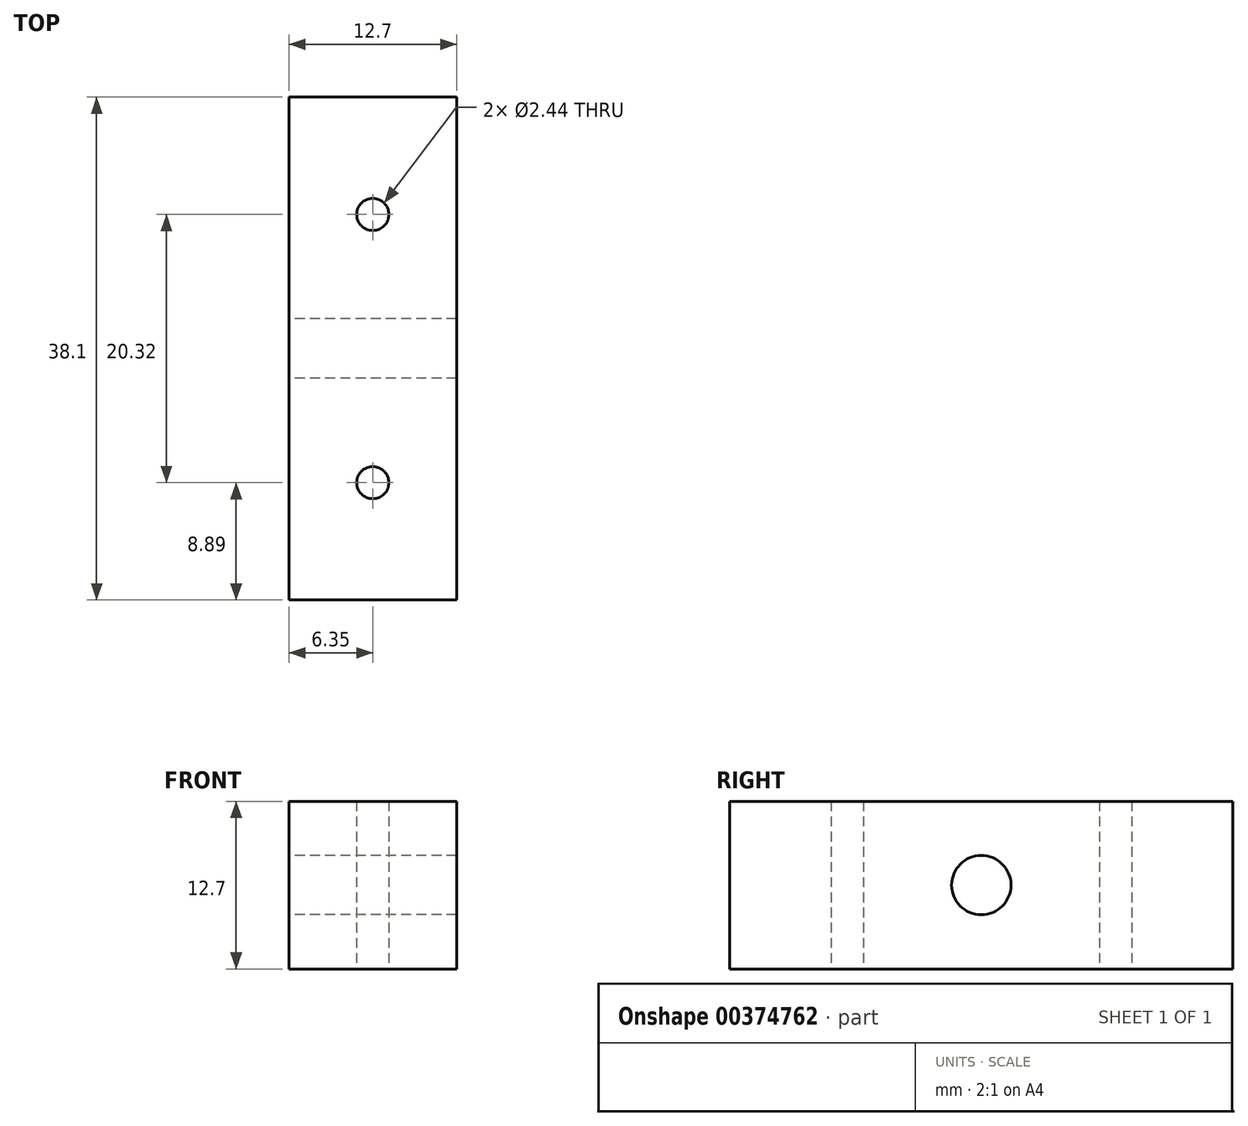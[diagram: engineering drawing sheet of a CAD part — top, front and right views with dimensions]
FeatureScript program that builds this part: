
annotation { "Feature Type Name" : "Feature", "Feature Type Description" : "" }
export const myFeature = defineFeature(function(context is Context, id is Id, definition is map)
    precondition{}
    {
        {
            var Q0;
            Q0=qCreatedBy(makeId("Top.planeOp"),FACE);
            var sketch = newSketch(context, id + "F0", { "sketchPlane" : qUnion([Q0])});
            skLineSegment(sketch, "E0.bottom", {"start": v(12.7, -19.05) * mm, "end": v(0, -19.05) * mm});
            skLineSegment(sketch, "E0.top", {"start": v(12.7, 19.05) * mm, "end": v(0, 19.05) * mm});
            skLineSegment(sketch, "E0.left", {"start": v(12.7, -19.05) * mm, "end": v(12.7, 19.05) * mm});
            skLineSegment(sketch, "E0.right", {"start": v(0, -19.05) * mm, "end": v(0, 19.05) * mm});
            skSolve(sketch);
        }
        {
            var Q0;
            Q0 = qSketchRegion(id + "F0", true);
            extrude(context, id + "F1", {"entities" : qUnion([Q0]), "depth" : 12.7 * mm});
        }
        {
            var Q0;
            Q0=qCreatedBy(makeId("Right.planeOp"),FACE);
            var sketch = newSketch(context, id + "F2", { "sketchPlane" : qUnion([Q0])});
            skPoint(sketch, "E1", {"position": v(0, 6.35) * mm});
            skSolve(sketch);
        }
        {
            var Q0;
            Q0=sQuery(id+"F2.wireOp",VERTEX,"E1");
            var Q1;
            Q1=makeQuery(id+"F1.opExtrude","SWEPT_BODY",BODY,{"disambiguationData":[OSD([sQuery(id+"F0.wireOp",EDGE,"E0.bottom"),sQuery(id+"F0.wireOp",EDGE,"E0.top"),sQuery(id+"F0.wireOp",EDGE,"E0.left"),sQuery(id+"F0.wireOp",EDGE,"E0.right")])]});
            hole(context, id + "F3", {"style" : HoleStyle.SIMPLE, "endStyle" : HoleEndStyle.THROUGH, "oppositeDirection" : true, "standardTappedOrClearance" : lookupTablePath({ "standard" : "ANSI", "fit" : "Normal (ASME)", "size" : "#8", "type" : "Clearance" }), "standardBlindInLast" : lookupTablePath({ "fit" : "Free", "standard" : "ANSI", "size" : "#8", "type" : "Clearance" }), "holeDiameter" : 4.5 * mm, "isTappedThrough" : true, "tappedDepth" : 12.7 * mm, "tapClearance" : 3, "locations" : qUnion([Q0]), "scope" : qUnion([Q1])});
        }
        {
            var Q0;
            Q0=qCreatedBy(makeId("Top.planeOp"),FACE);
            var sketch = newSketch(context, id + "F4", { "sketchPlane" : qUnion([Q0])});
            skPoint(sketch, "E2", {"position": v(6.35, 10.16) * mm});
            skPoint(sketch, "E3", {"position": v(6.35, -10.16) * mm});
            skSolve(sketch);
        }
        {
            var Q0;
            Q0=sQuery(id+"F4.wireOp",VERTEX,"E2");
            var Q1;
            Q1=sQuery(id+"F4.wireOp",VERTEX,"E3");
            var Q2;
            Q2=makeQuery(id+"F1.opExtrude","SWEPT_BODY",BODY,{"disambiguationData":[OSD([sQuery(id+"F0.wireOp",EDGE,"E0.bottom"),sQuery(id+"F0.wireOp",EDGE,"E0.top"),sQuery(id+"F0.wireOp",EDGE,"E0.left"),sQuery(id+"F0.wireOp",EDGE,"E0.right")])]});
            hole(context, id + "F5", {"style" : HoleStyle.SIMPLE, "endStyle" : HoleEndStyle.THROUGH, "oppositeDirection" : true, "standardTappedOrClearance" : lookupTablePath({ "standard" : "ANSI", "fit" : "Normal (ASME)", "size" : "#2", "type" : "Clearance" }), "standardBlindInLast" : lookupTablePath({ "fit" : "Free", "standard" : "ANSI", "size" : "#2", "type" : "Clearance" }), "holeDiameter" : 2.44 * mm, "isTappedThrough" : true, "tappedDepth" : 12.7 * mm, "tapClearance" : 3, "locations" : qUnion([Q0, Q1]), "scope" : qUnion([Q2])});
        }
    });
